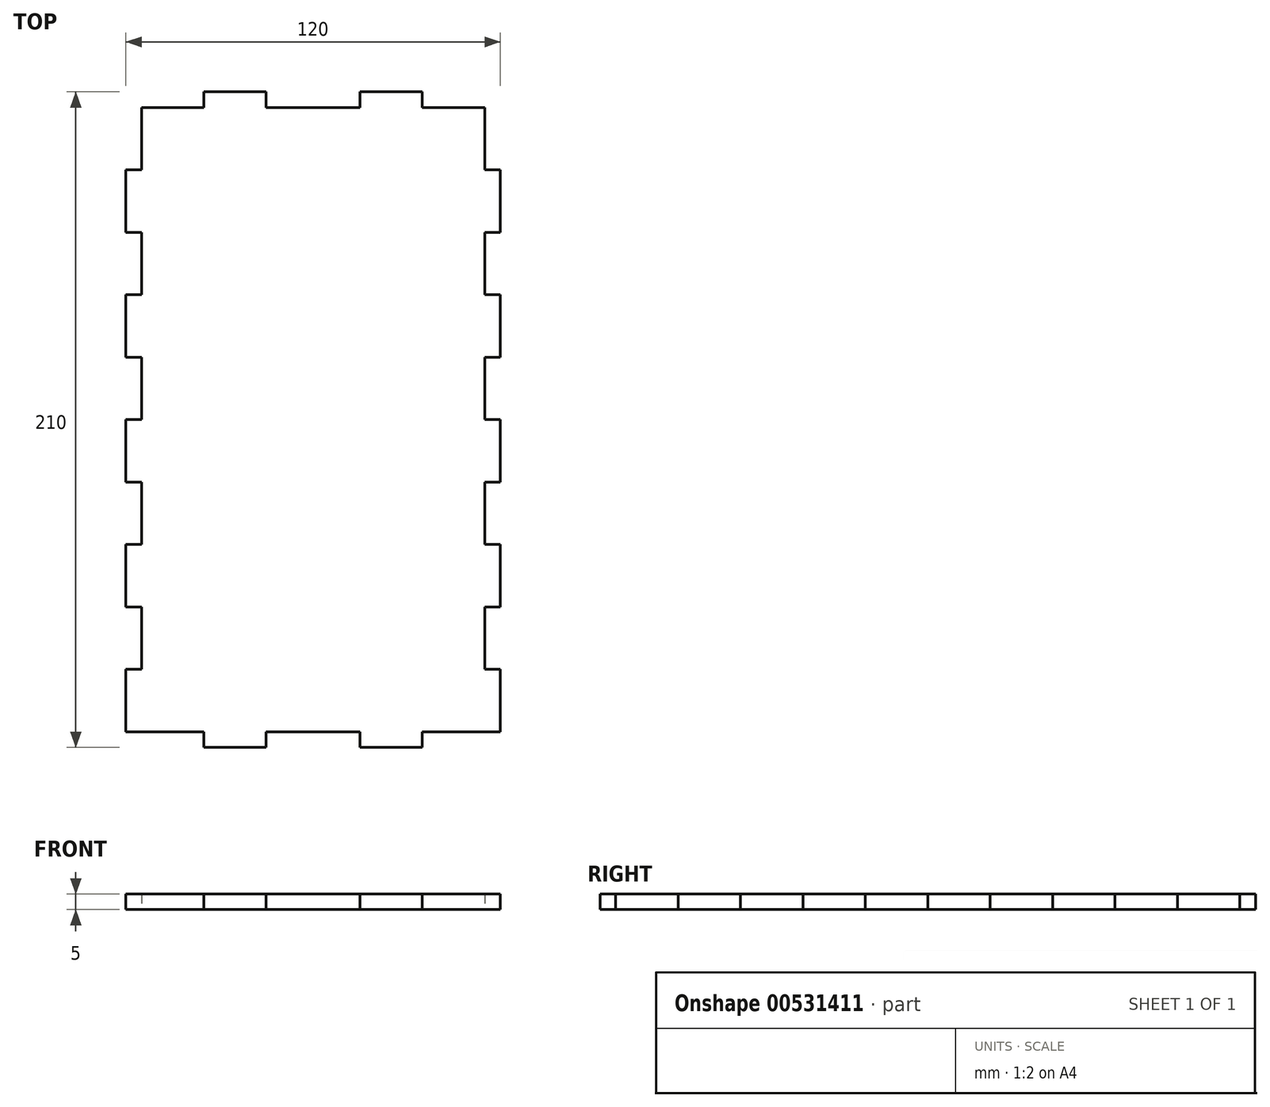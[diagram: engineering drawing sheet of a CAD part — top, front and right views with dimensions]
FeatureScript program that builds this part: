
annotation { "Feature Type Name" : "Feature", "Feature Type Description" : "" }
export const myFeature = defineFeature(function(context is Context, id is Id, definition is map)
    precondition{}
    {
        {
            var Q0;
            Q0=qCreatedBy(makeId("Top.planeOp"),FACE);
            var sketch = newSketch(context, id + "F0", { "sketchPlane" : qUnion([Q0])});
            skLineSegment(sketch, "E0.bottom", {"start": v(55, 100) * mm, "end": v(35, 100) * mm});
            skLineSegment(sketch, "E0.top", {"start": v(55, -100) * mm, "end": v(35, -100) * mm});
            skLineSegment(sketch, "E0.left", {"start": v(55, 100) * mm, "end": v(55, 80) * mm});
            skLineSegment(sketch, "E0.right", {"start": v(-55, 100) * mm, "end": v(-55, 80) * mm});
            skPoint(sketch, "E0.middle", {"position": v(0, 0) * mm});
            skLineSegment(sketch, "E1.bottom", {"start": v(-60, 105) * mm, "end": v(60, 105) * mm, "construction": true});
            skLineSegment(sketch, "E1.top", {"start": v(-60, -105) * mm, "end": v(60, -105) * mm, "construction": true});
            skLineSegment(sketch, "E1.left", {"start": v(-60, 105) * mm, "end": v(-60, -105) * mm, "construction": true});
            skLineSegment(sketch, "E1.right", {"start": v(60, 105) * mm, "end": v(60, -105) * mm, "construction": true});
            skLineSegment(sketch, "E2", {"start": v(-35, 100) * mm, "end": v(-35, 105) * mm});
            skLineSegment(sketch, "E3", {"start": v(-35, 105) * mm, "end": v(-15, 105) * mm});
            skLineSegment(sketch, "E4", {"start": v(-15, 105) * mm, "end": v(-15, 100) * mm});
            skLineSegment(sketch, "E5.MirrorCS", {"start": v(15, 105) * mm, "end": v(15, 100) * mm});
            skLineSegment(sketch, "E6.MirrorCS", {"start": v(35, 100) * mm, "end": v(35, 105) * mm});
            skLineSegment(sketch, "E7", {"start": v(15, 105) * mm, "end": v(35, 105) * mm});
            skLineSegment(sketch, "E8.trimOffspring", {"start": v(-35, 100) * mm, "end": v(-55, 100) * mm});
            skLineSegment(sketch, "E9.trimOffspring", {"start": v(15, 100) * mm, "end": v(-15, 100) * mm});
            skLineSegment(sketch, "E10.MirrorCS", {"start": v(-35, -100) * mm, "end": v(-35, -105) * mm});
            skLineSegment(sketch, "E11.MirrorCS", {"start": v(-15, -105) * mm, "end": v(-15, -100) * mm});
            skLineSegment(sketch, "E12.MirrorCS", {"start": v(15, -105) * mm, "end": v(15, -100) * mm});
            skLineSegment(sketch, "E13.MirrorCS", {"start": v(35, -100) * mm, "end": v(35, -105) * mm});
            skLineSegment(sketch, "E14", {"start": v(-35, -105) * mm, "end": v(-15, -105) * mm});
            skLineSegment(sketch, "E15", {"start": v(15, -105) * mm, "end": v(35, -105) * mm});
            skLineSegment(sketch, "E16.trimOffspring", {"start": v(-35, -100) * mm, "end": v(-55, -100) * mm});
            skLineSegment(sketch, "E17.trimOffspring", {"start": v(15, -100) * mm, "end": v(-15, -100) * mm});
            skLineSegment(sketch, "E18", {"start": v(-60, 20) * mm, "end": v(-55, 20) * mm});
            skLineSegment(sketch, "E19", {"start": v(-60, 20) * mm, "end": v(-60, 40) * mm});
            skLineSegment(sketch, "E20", {"start": v(-60, 40) * mm, "end": v(-55, 40) * mm});
            skLineSegment(sketch, "E21", {"start": v(-55, 60) * mm, "end": v(-60, 60) * mm});
            skLineSegment(sketch, "E22", {"start": v(-60, 60) * mm, "end": v(-60, 80) * mm});
            skLineSegment(sketch, "E23", {"start": v(-60, 80) * mm, "end": v(-55, 80) * mm});
            skLineSegment(sketch, "E24.trimOffspring", {"start": v(-55, 60) * mm, "end": v(-55, 40) * mm});
            skLineSegment(sketch, "E25.trimOffspring", {"start": v(-55, 20) * mm, "end": v(-55, 0) * mm});
            skLineSegment(sketch, "E26.MirrorCS", {"start": v(-60, -20) * mm, "end": v(-55, -20) * mm});
            skLineSegment(sketch, "E27.MirrorCS", {"start": v(-60, -40) * mm, "end": v(-55, -40) * mm});
            skLineSegment(sketch, "E28.MirrorCS", {"start": v(-55, -60) * mm, "end": v(-60, -60) * mm});
            skLineSegment(sketch, "E29.MirrorCS", {"start": v(-60, -80) * mm, "end": v(-55, -80) * mm});
            skLineSegment(sketch, "E30.MirrorCS", {"start": v(60, -80) * mm, "end": v(55, -80) * mm});
            skLineSegment(sketch, "E31.MirrorCS", {"start": v(55, -60) * mm, "end": v(60, -60) * mm});
            skLineSegment(sketch, "E32.MirrorCS", {"start": v(60, -40) * mm, "end": v(55, -40) * mm});
            skLineSegment(sketch, "E33.MirrorCS", {"start": v(60, -20) * mm, "end": v(55, -20) * mm});
            skLineSegment(sketch, "E34.MirrorCS", {"start": v(60, 20) * mm, "end": v(55, 20) * mm});
            skLineSegment(sketch, "E35.MirrorCS", {"start": v(60, 40) * mm, "end": v(55, 40) * mm});
            skLineSegment(sketch, "E36.MirrorCS", {"start": v(55, 60) * mm, "end": v(60, 60) * mm});
            skLineSegment(sketch, "E37.MirrorCS", {"start": v(60, 80) * mm, "end": v(55, 80) * mm});
            skLineSegment(sketch, "E38", {"start": v(-60, -20) * mm, "end": v(-60, 0) * mm});
            skLineSegment(sketch, "E39", {"start": v(-60, 0) * mm, "end": v(-55, 0) * mm});
            skLineSegment(sketch, "E40", {"start": v(-60, -40) * mm, "end": v(-60, -60) * mm});
            skLineSegment(sketch, "E41", {"start": v(-55, -100) * mm, "end": v(-60, -100) * mm});
            skLineSegment(sketch, "E42", {"start": v(-60, -100) * mm, "end": v(-60, -80) * mm});
            skLineSegment(sketch, "E43.trimOffspring", {"start": v(-55, -60) * mm, "end": v(-55, -80) * mm});
            skLineSegment(sketch, "E44.trimOffspring", {"start": v(-55, -20) * mm, "end": v(-55, -40) * mm});
            skLineSegment(sketch, "E45", {"start": v(-55, 100) * mm, "end": v(-55, -100) * mm, "construction": true});
            skLineSegment(sketch, "E46", {"start": v(60, 80) * mm, "end": v(60, 60) * mm});
            skLineSegment(sketch, "E47", {"start": v(60, 40) * mm, "end": v(60, 20) * mm});
            skLineSegment(sketch, "E48", {"start": v(55, 0) * mm, "end": v(60, 0) * mm});
            skLineSegment(sketch, "E49", {"start": v(60, 0) * mm, "end": v(60, -20) * mm});
            skLineSegment(sketch, "E50", {"start": v(60, -40) * mm, "end": v(60, -60) * mm});
            skLineSegment(sketch, "E51", {"start": v(60, -80) * mm, "end": v(60, -100) * mm});
            skLineSegment(sketch, "E52", {"start": v(60, -100) * mm, "end": v(55, -100) * mm});
            skLineSegment(sketch, "E53.trimOffspring", {"start": v(55, -60) * mm, "end": v(55, -80) * mm});
            skLineSegment(sketch, "E54.trimOffspring", {"start": v(55, -20) * mm, "end": v(55, -40) * mm});
            skLineSegment(sketch, "E55.trimOffspring", {"start": v(55, 20) * mm, "end": v(55, 0) * mm});
            skLineSegment(sketch, "E56.trimOffspring", {"start": v(55, 60) * mm, "end": v(55, 40) * mm});
            skSolve(sketch);
        }
        {
            var Q0;
            Q0 = qSketchRegion(id + "F0", true);
            extrude(context, id + "F1", {"entities" : qUnion([Q0]), "depth" : 5 * mm, "offsetDistance" : 25 * mm});
        }
    });
